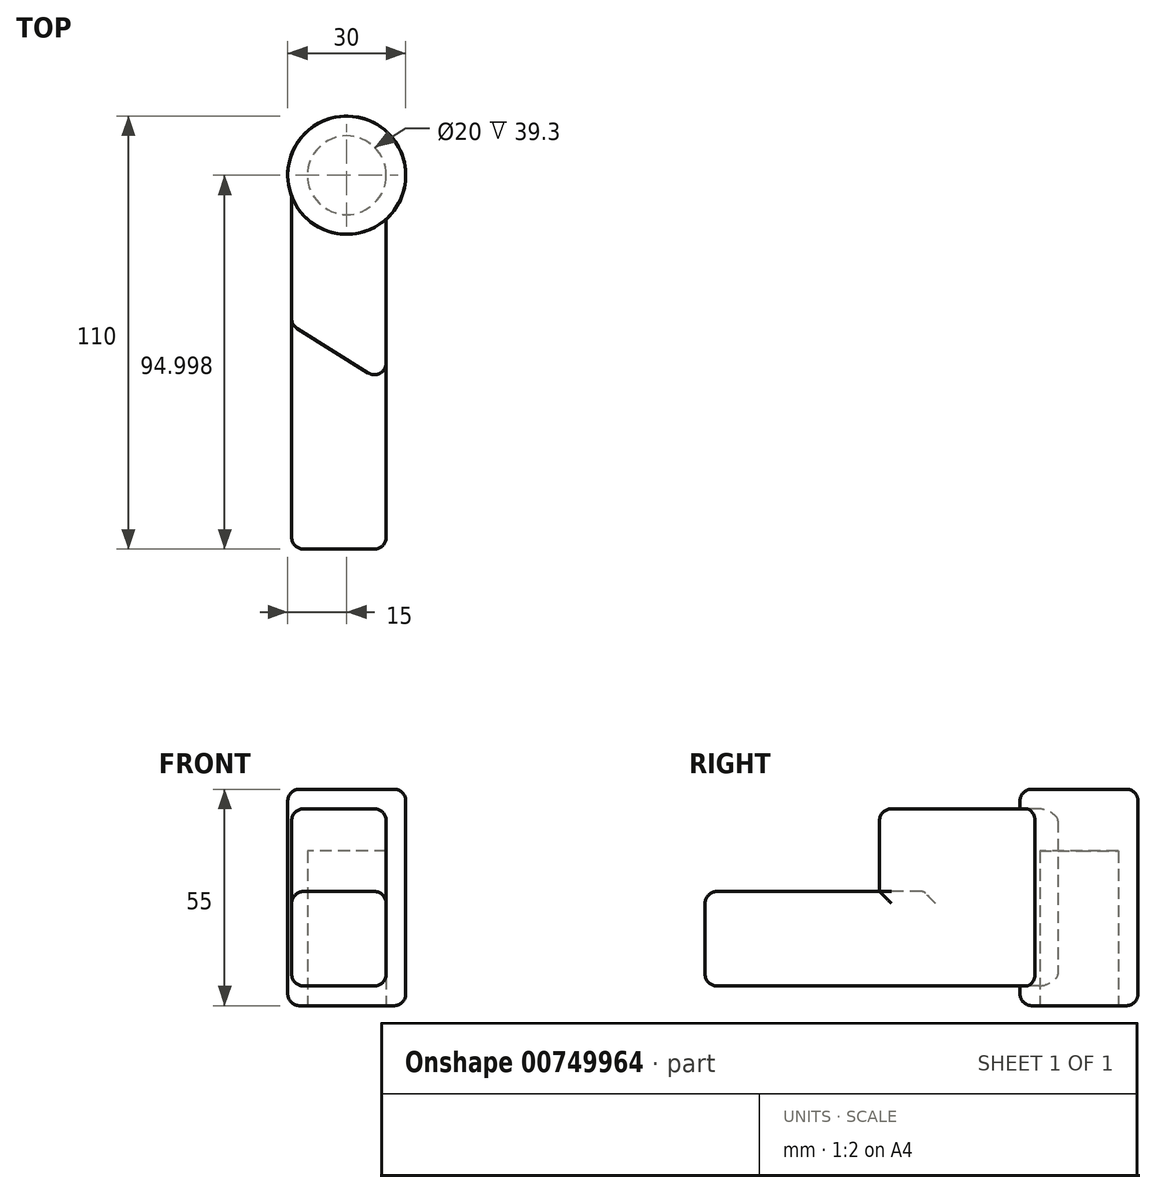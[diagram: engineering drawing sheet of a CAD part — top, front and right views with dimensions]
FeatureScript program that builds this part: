
annotation { "Feature Type Name" : "Feature", "Feature Type Description" : "" }
export const myFeature = defineFeature(function(context is Context, id is Id, definition is map)
    precondition{}
    {
        {
            var Q0;
            Q0=qCreatedBy(makeId("Top.planeOp"),FACE);
            var sketch = newSketch(context, id + "F0", { "sketchPlane" : qUnion([Q0])});
            skCircle(sketch, "E0", {"center": v(0, 34.13) * mm, "radius": 15 * mm});
            skCircle(sketch, "E1", {"center": v(0, 34.13) * mm, "radius": 10 * mm});
            skLineSegment(sketch, "E2", {"start": v(-14, 28.74) * mm, "end": v(-14, -60.87) * mm});
            skLineSegment(sketch, "E3", {"start": v(-14, -60.87) * mm, "end": v(10, -60.87) * mm});
            skLineSegment(sketch, "E4", {"start": v(10, -60.87) * mm, "end": v(10, 22.95) * mm});
            skLineSegment(sketch, "E5", {"start": v(-14, -3.99) * mm, "end": v(10, -18.96) * mm});
            skSolve(sketch);
        }
        {
            var Q0;
            Q0=makeQuery(id+"F0.imprint","IMPRINT",FACE,{"disambiguationData":[TD([[makeQuery(id+"F0.imprint","IMPRINT",EDGE,{"derivedFrom":sQuery(id+"F0.wireOp",EDGE,"E1")}),-1.0]])]});
            var Q1;
            Q1=makeQuery(id+"F0.imprint","IMPRINT",FACE,{"disambiguationData":[TD([[makeQuery(id+"F0.imprint","IMPRINT",EDGE,{"derivedFrom":sQuery(id+"F0.wireOp",EDGE,"E1")}),1.0]])]});
            extrude(context, id + "F1", {"entities" : qUnion([Q0, Q1]), "depth" : 50 * mm, "offsetDistance" : 25 * mm});
        }
        {
            var Q0;
            Q0=makeQuery(id+"F0.imprint","IMPRINT",FACE,{"disambiguationData":[TD([[makeQuery(id+"F0.imprint","IMPRINT",EDGE,{"derivedFrom":sQuery(id+"F0.wireOp",EDGE,"E1")}),-1.0]])]});
            var Q1;
            Q1=makeQuery(id+"F0.imprint","IMPRINT",FACE,{"disambiguationData":[TD([[makeQuery(id+"F0.imprint","IMPRINT",EDGE,{"derivedFrom":sQuery(id+"F0.wireOp",EDGE,"E1")}),1.0]])]});
            extrude(context, id + "F2", {"entities" : qUnion([Q0, Q1]), "operationType" : NewBodyOperationType.ADD, "oppositeDirection" : true, "depth" : 5 * mm, "offsetDistance" : 25 * mm});
        }
        {
            var Q0;
            {var subQ5=sQuery(id+"F0.wireOp",EDGE,"E5");Q0=makeQuery(id+"F0.imprint","IMPRINT",FACE,{"disambiguationData":[TD([[makeQuery(id+"F0.imprint","IMPRINT",EDGE,{"derivedFrom":subQ5}),1.0]])]});}
            extrude(context, id + "F3", {"entities" : qUnion([Q0]), "operationType" : NewBodyOperationType.ADD, "depth" : 45 * mm, "offsetDistance" : 25 * mm});
        }
        {
            var Q0;
            {var subQ0=sQuery(id+"F0.wireOp",EDGE,"E3");Q0=makeQuery(id+"F0.imprint","IMPRINT",FACE,{"disambiguationData":[TD([[makeQuery(id+"F0.imprint","IMPRINT",EDGE,{"derivedFrom":subQ0}),1.0]])]});}
            extrude(context, id + "F4", {"entities" : qUnion([Q0]), "operationType" : NewBodyOperationType.ADD, "depth" : 24 * mm, "offsetDistance" : 25 * mm});
        }
        {
            var Q0;
            Q0=makeQuery(id+"F0.imprint","IMPRINT",FACE,{"disambiguationData":[TD([[makeQuery(id+"F0.imprint","IMPRINT",EDGE,{"derivedFrom":sQuery(id+"F0.wireOp",EDGE,"E1")}),1.0]])]});
            extrude(context, id + "F5", {"entities" : qUnion([Q0]), "operationType" : NewBodyOperationType.REMOVE, "endBound" : BoundingType.SYMMETRIC, "depth" : 68.6 * mm, "offsetDistance" : 25 * mm});
        }
        {
            var Q0;
            Q0=makeQuery(id+"F3.opExtrude","CAP_EDGE",EDGE,{"disambiguationData":[OSD([sQuery(id+"F0.wireOp",EDGE,"E2")])],"isStart":false});
            var Q1;
            Q1=makeQuery(id+"F3.opExtrude","SWEPT_EDGE",EDGE,{"disambiguationData":[OSD([sQuery(id+"F0.wireOp",EDGE,"E2"),sQuery(id+"F0.wireOp",EDGE,"E5")])]});
            var Q2;
            Q2=makeQuery(id+"F3.opExtrude","CAP_EDGE",EDGE,{"disambiguationData":[OSD([sQuery(id+"F0.wireOp",EDGE,"E5")])],"isStart":false});
            var Q3;
            Q3=makeQuery(id+"F3.opExtrude","CAP_EDGE",EDGE,{"disambiguationData":[OSD([sQuery(id+"F0.wireOp",EDGE,"E4")])],"isStart":false});
            var Q4;
            Q4=makeQuery(id+"F4.opExtrude","CAP_EDGE",EDGE,{"disambiguationData":[OSD([sQuery(id+"F0.wireOp",EDGE,"E2")])],"isStart":false});
            var Q5;
            Q5=makeQuery(id+"F4.opExtrude","CAP_EDGE",EDGE,{"disambiguationData":[OSD([sQuery(id+"F0.wireOp",EDGE,"E4")])],"isStart":false});
            var Q6;
            Q6=makeQuery(id+"F4.opExtrude","CAP_EDGE",EDGE,{"disambiguationData":[OSD([sQuery(id+"F0.wireOp",EDGE,"E3")])],"isStart":false});
            var Q7;
            Q7=makeQuery(id+"F4.opExtrude","SWEPT_EDGE",EDGE,{"disambiguationData":[OSD([sQuery(id+"F0.wireOp",EDGE,"E3"),sQuery(id+"F0.wireOp",EDGE,"E4")])]});
            var Q8;
            Q8=makeQuery(id+"F4.opExtrude","SWEPT_EDGE",EDGE,{"disambiguationData":[OSD([sQuery(id+"F0.wireOp",EDGE,"E2"),sQuery(id+"F0.wireOp",EDGE,"E3")])]});
            var Q9;
            Q9=makeQuery(id+"F4.opExtrude","CAP_EDGE",EDGE,{"disambiguationData":[OSD([sQuery(id+"F0.wireOp",EDGE,"E3")])],"isStart":true});
            var Q10;
            {var subQ0=sQuery(id+"F0.wireOp",EDGE,"E2");Q10=makeQuery(id+"F4.boolean.opBoolean","MERGE",EDGE,{"derivedFrom":[makeQuery(id+"F3.opExtrude","CAP_EDGE",EDGE,{"disambiguationData":[OSD([subQ0])],"isStart":true}),makeQuery(id+"F4.opExtrude","CAP_EDGE",EDGE,{"disambiguationData":[OSD([subQ0])],"isStart":true})]});}
            var Q11;
            Q11=makeQuery(id+"F3.opExtrude","SWEPT_EDGE",EDGE,{"disambiguationData":[OSD([sQuery(id+"F0.wireOp",EDGE,"E4"),sQuery(id+"F0.wireOp",EDGE,"E5")])]});
            var Q12;
            {var subQ0=sQuery(id+"F0.wireOp",EDGE,"E4");Q12=makeQuery(id+"F4.boolean.opBoolean","MERGE",EDGE,{"derivedFrom":[makeQuery(id+"F3.opExtrude","CAP_EDGE",EDGE,{"disambiguationData":[OSD([subQ0])],"isStart":true}),makeQuery(id+"F4.opExtrude","CAP_EDGE",EDGE,{"disambiguationData":[OSD([subQ0])],"isStart":true})]});}
            var Q13;
            Q13=makeQuery(id+"F2.opExtrude","CAP_EDGE",EDGE,{"disambiguationData":[OSD([sQuery(id+"F0.wireOp",EDGE,"E0")])],"isStart":false});
            var Q14;
            Q14=makeQuery(id+"F1.opExtrude","CAP_EDGE",EDGE,{"disambiguationData":[OSD([sQuery(id+"F0.wireOp",EDGE,"E0")])],"isStart":false});
            fillet(context, id + "F6", {"entities" : qUnion([Q0, Q1, Q2, Q3, Q4, Q5, Q6, Q7, Q8, Q9, Q10, Q11, Q12, Q13, Q14]), "radius" : 3 * mm, "tangentPropagation" : true, "allowEdgeOverflow" : false});
        }
    });
